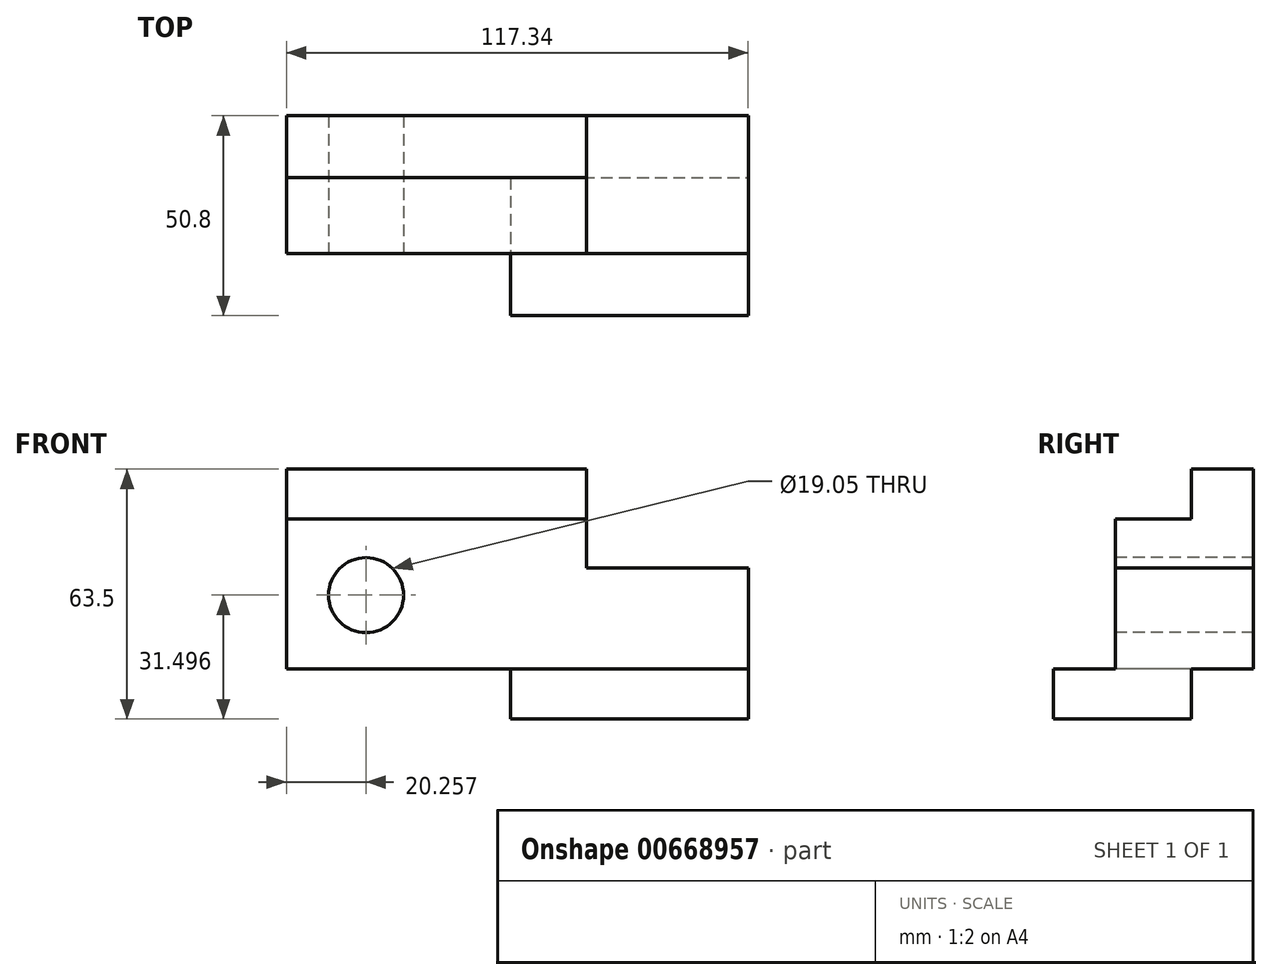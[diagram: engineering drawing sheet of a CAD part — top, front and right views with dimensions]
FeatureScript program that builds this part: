
annotation { "Feature Type Name" : "Feature", "Feature Type Description" : "" }
export const myFeature = defineFeature(function(context is Context, id is Id, definition is map)
    precondition{}
    {
        {
            var Q0;
            Q0=qCreatedBy(makeId("Front.planeOp"),FACE);
            var sketch = newSketch(context, id + "F0", { "sketchPlane" : qUnion([Q0])});
            skLineSegment(sketch, "E0.bottom", {"start": v(-58.67, 31.75) * mm, "end": v(58.67, 31.75) * mm});
            skLineSegment(sketch, "E0.top", {"start": v(-58.67, -31.75) * mm, "end": v(58.67, -31.75) * mm});
            skLineSegment(sketch, "E0.left", {"start": v(-58.67, 31.75) * mm, "end": v(-58.67, -31.75) * mm});
            skLineSegment(sketch, "E0.right", {"start": v(58.67, 31.75) * mm, "end": v(58.67, -31.75) * mm});
            skPoint(sketch, "E0.middle", {"position": v(0, 0) * mm});
            skSolve(sketch);
        }
        {
            var Q0;
            Q0 = qSketchRegion(id + "F0", true);
            extrude(context, id + "F1", {"entities" : qUnion([Q0]), "depth" : 50.8 * mm, "offsetDistance" : 25.4 * mm});
        }
        {
            var Q0;
            Q0=makeQuery(id+"F1.opExtrude","SWEPT_FACE",FACE,{"disambiguationData":[OSD([sQuery(id+"F0.wireOp",EDGE,"E0.left")])]});
            var sketch = newSketch(context, id + "F2", { "sketchPlane" : qUnion([Q0])});
            skLineSegment(sketch, "E1.bottom", {"start": v(50.8, 31.75) * mm, "end": v(15.75, 31.75) * mm});
            skLineSegment(sketch, "E1.top", {"start": v(50.8, 19.05) * mm, "end": v(15.75, 19.05) * mm});
            skLineSegment(sketch, "E1.left", {"start": v(50.8, 31.75) * mm, "end": v(50.8, 19.05) * mm});
            skLineSegment(sketch, "E1.right", {"start": v(15.75, 31.75) * mm, "end": v(15.75, 19.05) * mm});
            skSolve(sketch);
        }
        {
            var Q0;
            Q0 = qSketchRegion(id + "F2", true);
            extrude(context, id + "F3", {"entities" : qUnion([Q0]), "operationType" : NewBodyOperationType.REMOVE, "endBound" : BoundingType.THROUGH_ALL, "oppositeDirection" : true, "depth" : 25.4 * mm, "offsetDistance" : 25.4 * mm});
        }
        {
            var Q0;
            Q0=makeQuery(id+"F1.opExtrude","SWEPT_FACE",FACE,{"disambiguationData":[OSD([sQuery(id+"F0.wireOp",EDGE,"E0.right")])]});
            var sketch = newSketch(context, id + "F4", { "sketchPlane" : qUnion([Q0])});
            skLineSegment(sketch, "E2.bottom", {"start": v(-50.8, -19.05) * mm, "end": v(-35.05, -19.05) * mm});
            skLineSegment(sketch, "E2.top", {"start": v(-50.8, 19.05) * mm, "end": v(-35.05, 19.05) * mm});
            skLineSegment(sketch, "E2.left", {"start": v(-50.8, -19.05) * mm, "end": v(-50.8, 19.05) * mm});
            skLineSegment(sketch, "E2.right", {"start": v(-35.05, -19.05) * mm, "end": v(-35.05, 19.05) * mm});
            skSolve(sketch);
        }
        {
            var Q0;
            Q0 = qSketchRegion(id + "F4", true);
            extrude(context, id + "F5", {"entities" : qUnion([Q0]), "operationType" : NewBodyOperationType.REMOVE, "endBound" : BoundingType.THROUGH_ALL, "depth" : 25.4 * mm, "offsetDistance" : 25.4 * mm});
        }
        {
            var Q0;
            Q0 = qSketchRegion(id + "F4", true);
            extrude(context, id + "F6", {"entities" : qUnion([Q0]), "operationType" : NewBodyOperationType.REMOVE, "endBound" : BoundingType.THROUGH_ALL, "oppositeDirection" : true, "depth" : 25.4 * mm, "offsetDistance" : 25.4 * mm});
        }
        {
            var Q0;
            Q0=makeQuery(id+"F6.boolean.opBoolean","COPY",FACE,{"derivedFrom":makeQuery(id+"F6.opExtrude","SWEPT_FACE",FACE,{"disambiguationData":[OSD([sQuery(id+"F4.wireOp",EDGE,"E2.right")])]})});
            var sketch = newSketch(context, id + "F7", { "sketchPlane" : qUnion([Q0])});
            skLineSegment(sketch, "E3.bottom", {"start": v(58.67, 32.09) * mm, "end": v(17.53, 32.09) * mm});
            skLineSegment(sketch, "E3.top", {"start": v(58.67, 6.65) * mm, "end": v(17.53, 6.65) * mm});
            skLineSegment(sketch, "E3.left", {"start": v(58.67, 32.09) * mm, "end": v(58.67, 6.65) * mm});
            skLineSegment(sketch, "E3.right", {"start": v(17.53, 32.09) * mm, "end": v(17.53, 6.65) * mm});
            skSolve(sketch);
        }
        {
            var Q0;
            Q0 = qSketchRegion(id + "F7", true);
            extrude(context, id + "F8", {"entities" : qUnion([Q0]), "operationType" : NewBodyOperationType.REMOVE, "endBound" : BoundingType.THROUGH_ALL, "oppositeDirection" : true, "depth" : 25.4 * mm, "offsetDistance" : 25.4 * mm});
        }
        {
            var Q0;
            Q0=makeQuery(id+"F1.opExtrude","CAP_FACE",FACE,{"disambiguationData":[OSD([sQuery(id+"F0.wireOp",EDGE,"E0.bottom"),sQuery(id+"F0.wireOp",EDGE,"E0.top"),sQuery(id+"F0.wireOp",EDGE,"E0.left"),sQuery(id+"F0.wireOp",EDGE,"E0.right")])],"isStart":false});
            var sketch = newSketch(context, id + "F9", { "sketchPlane" : qUnion([Q0])});
            skLineSegment(sketch, "E4.bottom", {"start": v(-58.67, -31.75) * mm, "end": v(-1.78, -31.75) * mm});
            skLineSegment(sketch, "E4.top", {"start": v(-58.67, -19.05) * mm, "end": v(-1.78, -19.05) * mm});
            skLineSegment(sketch, "E4.left", {"start": v(-58.67, -31.75) * mm, "end": v(-58.67, -19.05) * mm});
            skLineSegment(sketch, "E4.right", {"start": v(-1.78, -31.75) * mm, "end": v(-1.78, -19.05) * mm});
            skSolve(sketch);
        }
        {
            var Q0;
            Q0 = qSketchRegion(id + "F9", true);
            extrude(context, id + "F10", {"entities" : qUnion([Q0]), "operationType" : NewBodyOperationType.REMOVE, "endBound" : BoundingType.THROUGH_ALL, "oppositeDirection" : true, "depth" : 25.4 * mm, "offsetDistance" : 25.4 * mm});
        }
        {
            var Q0;
            Q0=makeQuery(id+"F1.opExtrude","SWEPT_FACE",FACE,{"disambiguationData":[OSD([sQuery(id+"F0.wireOp",EDGE,"E0.right")])]});
            var sketch = newSketch(context, id + "F11", { "sketchPlane" : qUnion([Q0])});
            skLineSegment(sketch, "E5.bottom", {"start": v(0, -31.75) * mm, "end": v(-15.75, -31.75) * mm});
            skLineSegment(sketch, "E5.top", {"start": v(0, -19.05) * mm, "end": v(-15.75, -19.05) * mm});
            skLineSegment(sketch, "E5.left", {"start": v(0, -31.75) * mm, "end": v(0, -19.05) * mm});
            skLineSegment(sketch, "E5.right", {"start": v(-15.75, -31.75) * mm, "end": v(-15.75, -19.05) * mm});
            skSolve(sketch);
        }
        {
            var Q0;
            Q0 = qSketchRegion(id + "F11", true);
            extrude(context, id + "F12", {"entities" : qUnion([Q0]), "operationType" : NewBodyOperationType.REMOVE, "endBound" : BoundingType.THROUGH_ALL, "oppositeDirection" : true, "depth" : 25.4 * mm, "offsetDistance" : 25.4 * mm});
        }
        {
            var Q0;
            Q0=makeQuery(id+"F6.boolean.opBoolean","COPY",FACE,{"derivedFrom":makeQuery(id+"F6.opExtrude","SWEPT_FACE",FACE,{"disambiguationData":[OSD([sQuery(id+"F4.wireOp",EDGE,"E2.right")])]})});
            var sketch = newSketch(context, id + "F13", { "sketchPlane" : qUnion([Q0])});
            skCircle(sketch, "E6", {"center": v(-38.41, -0.25) * mm, "radius": 9.53 * mm});
            skSolve(sketch);
        }
        {
            var Q0;
            Q0 = qSketchRegion(id + "F13", true);
            extrude(context, id + "F14", {"entities" : qUnion([Q0]), "operationType" : NewBodyOperationType.REMOVE, "endBound" : BoundingType.THROUGH_ALL, "oppositeDirection" : true, "depth" : 25.4 * mm, "offsetDistance" : 25.4 * mm});
        }
    });
